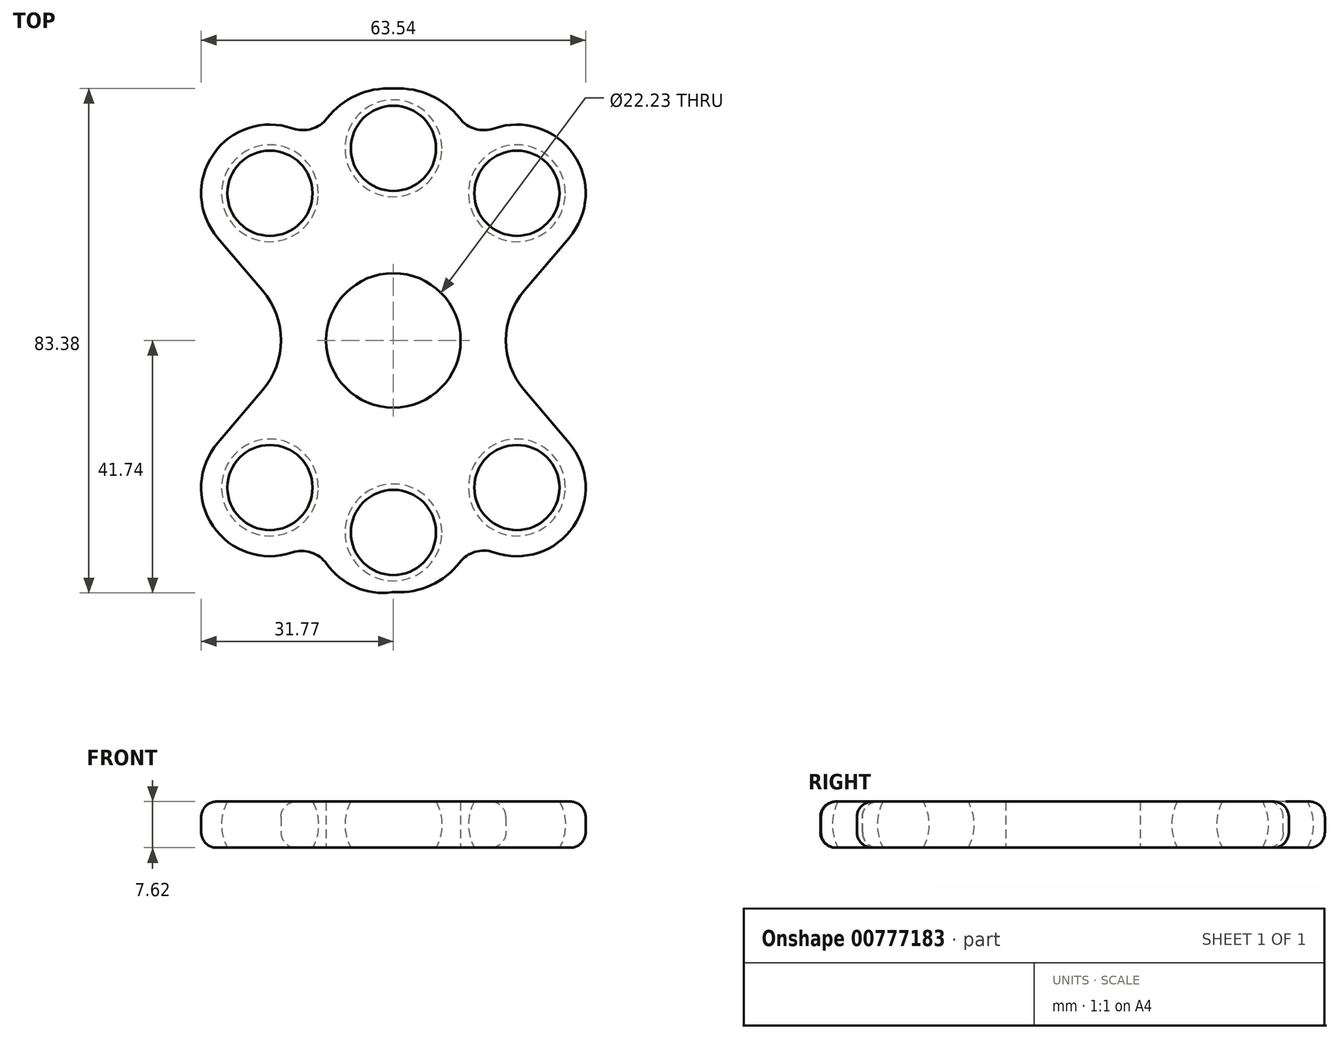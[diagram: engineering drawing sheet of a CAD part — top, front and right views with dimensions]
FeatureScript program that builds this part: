
annotation { "Feature Type Name" : "Feature", "Feature Type Description" : "" }
export const myFeature = defineFeature(function(context is Context, id is Id, definition is map)
    precondition{}
    {
        {
            var Q0;
            Q0=qCreatedBy(makeId("Top.planeOp"),FACE);
            var sketch = newSketch(context, id + "F0", { "sketchPlane" : qUnion([Q0])});
            skLineSegment(sketch, "E0", {"start": v(0, 31.75) * mm, "end": v(0, 0) * mm, "construction": true});
            skLineSegment(sketch, "E1", {"start": v(0, 0) * mm, "end": v(42.14, 0) * mm, "construction": true});
            skLineSegment(sketch, "E2", {"start": v(0, 31.75) * mm, "end": v(0, 57.84) * mm, "construction": true});
            skLineSegment(sketch, "E3", {"start": v(0, 0) * mm, "end": v(20.4, 24.32) * mm, "construction": true});
            skCircle(sketch, "E4", {"center": v(0, 0) * mm, "radius": 11.11 * mm});
            skArc(sketch, "E5", {"start": v(0, 23.75) * mm, "mid": v(8, 31.75) * mm, "end": v(0, 39.75) * mm, "construction": true});
            skCircle(sketch, "E6", {"center": v(20.4, 24.32) * mm, "radius": 8 * mm, "construction": true});
            skArc(sketch, "E7", {"start": v(29.05, 16.95) * mm, "mid": v(28.4, 32.38) * mm, "end": v(12.97, 32.9) * mm});
            skLineSegment(sketch, "E8", {"start": v(29.05, 16.95) * mm, "end": v(14.6, 0) * mm});
            skArc(sketch, "E9.MirrorCS", {"start": v(0, 23.75) * mm, "mid": v(-8, 31.75) * mm, "end": v(0, 39.75) * mm, "construction": true});
            skArc(sketch, "E10.MirrorC", {"start": v(-29.05, 16.95) * mm, "mid": v(-28.4, 32.38) * mm, "end": v(-12.97, 32.9) * mm});
            skCircle(sketch, "E11.MirrorC", {"center": v(-20.4, 24.32) * mm, "radius": 8 * mm, "construction": true});
            skLineSegment(sketch, "E12.MirrorCS", {"start": v(-29.05, 16.95) * mm, "end": v(-14.6, 0) * mm});
            skLineSegment(sketch, "E13.MirrorCS", {"start": v(29.05, -16.95) * mm, "end": v(14.6, 0) * mm});
            skLineSegment(sketch, "E14.MirrorCS", {"start": v(-29.05, -16.95) * mm, "end": v(-14.6, 0) * mm});
            skArc(sketch, "E15.MirrorC", {"start": v(-29.05, -16.95) * mm, "mid": v(-28.36, -32.43) * mm, "end": v(-12.87, -32.82) * mm});
            skArc(sketch, "E16.MirrorCS", {"start": v(-12.87, -32.82) * mm, "mid": v(-8.17, -39.75) * mm, "end": v(0, -41.6) * mm});
            skArc(sketch, "E17.MirrorC", {"start": v(29.05, -16.95) * mm, "mid": v(28.4, -32.38) * mm, "end": v(12.97, -32.9) * mm});
            skPoint(sketch, "E18.orphan", {"position": v(-8.46, 7.2) * mm});
            skPoint(sketch, "E19.orphan", {"position": v(-8.46, -7.2) * mm});
            skPoint(sketch, "E20.orphan", {"position": v(8.46, -7.2) * mm});
            skPoint(sketch, "E21.orphan", {"position": v(8.46, 7.2) * mm});
            skArc(sketch, "E22.trimOffspring", {"start": v(-12.97, 32.9) * mm, "mid": v(-7.98, 39.49) * mm, "end": v(0, 41.6) * mm});
            skArc(sketch, "E23.trimOffspring", {"start": v(12.97, 32.9) * mm, "mid": v(7.98, 39.49) * mm, "end": v(0, 41.6) * mm});
            skArc(sketch, "E24.trimOffspring", {"start": v(12.97, -32.9) * mm, "mid": v(7.98, -39.49) * mm, "end": v(0, -41.6) * mm});
            skPoint(sketch, "E25.MirrorCS.start.orphan", {"position": v(0, -19.05) * mm});
            skPoint(sketch, "E26.MirrorCS.start.orphan", {"position": v(0, 19.05) * mm});
            skSolve(sketch);
        }
        {
            var Q0;
            Q0=qSketchRegion(id+"F0",true);
            extrude(context, id + "F1", {"entities" : qUnion([Q0]), "endBound" : BoundingType.SYMMETRIC, "depth" : 7.62 * mm, "offsetDistance" : 25.4 * mm});
        }
        {
            var Q0;
            Q0=qCreatedBy(makeId("Front.planeOp"),FACE);
            var sketch = newSketch(context, id + "F2", { "sketchPlane" : qUnion([Q0])});
            skLineSegment(sketch, "E27", {"start": v(0, 0) * mm, "end": v(0, 93.09) * mm});
            skSolve(sketch);
        }
        {
            var Q0;
            Q0=sQuery(id+"F0.wireOp",VERTEX,"E3.end");
            var Q1;
            Q1=sQuery(id+"F2.wireOp",VERTEX,"E27.end");
            var Q2;
            Q2=sQuery(id+"F0.wireOp",VERTEX,"E0.end");
            cPlane(context, id + "F3", {"entities" : qUnion([Q0, Q1, Q2]), "cplaneType" : CPlaneType.THREE_POINT, "offset" : 25.4 * mm, "width" : 152.4 * mm, "height" : 152.4 * mm});
        }
        {
            var Q0;
            Q0=qCreatedBy(id+"F3.planeOp",FACE);
            var sketch = newSketch(context, id + "F4", { "sketchPlane" : qUnion([Q0])});
            skLineSegment(sketch, "E28", {"start": v(-31.75, 0) * mm, "end": v(-31.75, 45.58) * mm, "construction": true});
            skLineSegment(sketch, "E29", {"start": v(-31.75, 8) * mm, "end": v(-31.75, -8) * mm});
            skArc(sketch, "E30", {"start": v(-31.75, 8) * mm, "mid": v(-39.75, 0) * mm, "end": v(-31.75, -8) * mm});
            skSolve(sketch);
        }
        {
            var Q0;
            Q0=qSketchRegion(id+"F4",true);
            var Q1;
            Q1=sQuery(id+"F4.wireOp",EDGE,"E28");
            revolve(context, id + "F5", {"surfaceOperationType" : NewSurfaceOperationType.NEW, "entities" : qUnion([Q0]), "axis" : qUnion([Q1]), "revolveType" : RevolveType.FULL});
        }
        {
            var Q0;
            Q0=qCreatedBy(makeId("Right.planeOp"),FACE);
            var sketch = newSketch(context, id + "F6", { "sketchPlane" : qUnion([Q0])});
            skLineSegment(sketch, "E31", {"start": v(31.75, 0) * mm, "end": v(31.75, 41) * mm, "construction": true});
            skLineSegment(sketch, "E32", {"start": v(31.75, 8) * mm, "end": v(31.75, -8) * mm});
            skArc(sketch, "E33", {"start": v(31.75, -8) * mm, "mid": v(39.75, 0) * mm, "end": v(31.75, 8) * mm});
            skSolve(sketch);
        }
        {
            var Q0;
            Q0=makeQuery(id+"F6.imprint","IMPRINT",FACE,{"disambiguationData":[TD([[makeQuery(id+"F6.imprint","IMPRINT",EDGE,{"derivedFrom":sQuery(id+"F6.wireOp",EDGE,"E32")}),1.0]])]});
            var Q1;
            Q1=sQuery(id+"F6.wireOp",EDGE,"E31");
            revolve(context, id + "F7", {"surfaceOperationType" : NewSurfaceOperationType.NEW, "entities" : qUnion([Q0]), "axis" : qUnion([Q1]), "revolveType" : RevolveType.FULL});
        }
        {
            var Q0;
            Q0=makeQuery(id+"F5.opRevolve","SWEPT_BODY",BODY,{"disambiguationData":[OSD([sQuery(id+"F4.wireOp",EDGE,"E29"),sQuery(id+"F4.wireOp",EDGE,"E30")])]});
            var Q1;
            Q1=qCreatedBy(makeId("Right.planeOp"),FACE);
            mirror(context, id + "F8", {"entities" : qUnion([Q0]), "mirrorPlane" : qUnion([Q1])});
        }
        {
            var Q0;
            Q0=makeQuery(id+"F8.opPattern","COPY",BODY,{"derivedFrom":makeQuery(id+"F5.opRevolve","SWEPT_BODY",BODY,{"disambiguationData":[OSD([sQuery(id+"F4.wireOp",EDGE,"E29"),sQuery(id+"F4.wireOp",EDGE,"E30")])]}),"instanceName":"1"});
            var Q1;
            Q1=makeQuery(id+"F7.opRevolve","SWEPT_BODY",BODY,{"disambiguationData":[OSD([sQuery(id+"F6.wireOp",EDGE,"E32"),sQuery(id+"F6.wireOp",EDGE,"E33")])]});
            var Q2;
            Q2=makeQuery(id+"F5.opRevolve","SWEPT_BODY",BODY,{"disambiguationData":[OSD([sQuery(id+"F4.wireOp",EDGE,"E29"),sQuery(id+"F4.wireOp",EDGE,"E30")])]});
            var Q3;
            Q3=qCreatedBy(makeId("Front.planeOp"),FACE);
            mirror(context, id + "F9", {"entities" : qUnion([Q0, Q1, Q2]), "mirrorPlane" : qUnion([Q3])});
        }
        {
            var Q0;
            Q0=makeQuery(id+"F9.opPattern","COPY",BODY,{"derivedFrom":makeQuery(id+"F8.opPattern","COPY",BODY,{"derivedFrom":makeQuery(id+"F5.opRevolve","SWEPT_BODY",BODY,{"disambiguationData":[OSD([sQuery(id+"F4.wireOp",EDGE,"E29"),sQuery(id+"F4.wireOp",EDGE,"E30")])]}),"instanceName":"1"}),"instanceName":"1"});
            var Q1;
            Q1=makeQuery(id+"F9.opPattern","COPY",BODY,{"derivedFrom":makeQuery(id+"F7.opRevolve","SWEPT_BODY",BODY,{"disambiguationData":[OSD([sQuery(id+"F6.wireOp",EDGE,"E32"),sQuery(id+"F6.wireOp",EDGE,"E33")])]}),"instanceName":"1"});
            var Q2;
            Q2=makeQuery(id+"F9.opPattern","COPY",BODY,{"derivedFrom":makeQuery(id+"F5.opRevolve","SWEPT_BODY",BODY,{"disambiguationData":[OSD([sQuery(id+"F4.wireOp",EDGE,"E29"),sQuery(id+"F4.wireOp",EDGE,"E30")])]}),"instanceName":"1"});
            var Q3;
            Q3=makeQuery(id+"F8.opPattern","COPY",BODY,{"derivedFrom":makeQuery(id+"F5.opRevolve","SWEPT_BODY",BODY,{"disambiguationData":[OSD([sQuery(id+"F4.wireOp",EDGE,"E29"),sQuery(id+"F4.wireOp",EDGE,"E30")])]}),"instanceName":"1"});
            var Q4;
            Q4=makeQuery(id+"F5.opRevolve","SWEPT_BODY",BODY,{"disambiguationData":[OSD([sQuery(id+"F4.wireOp",EDGE,"E29"),sQuery(id+"F4.wireOp",EDGE,"E30")])]});
            var Q5;
            Q5=makeQuery(id+"F7.opRevolve","SWEPT_BODY",BODY,{"disambiguationData":[OSD([sQuery(id+"F6.wireOp",EDGE,"E32"),sQuery(id+"F6.wireOp",EDGE,"E33")])]});
            var Q6;
            Q6=makeQuery(id+"F1.opExtrude","SWEPT_BODY",BODY,{"disambiguationData":[OSD([sQuery(id+"F0.wireOp",EDGE,"E4"),sQuery(id+"F0.wireOp",EDGE,"E7"),sQuery(id+"F0.wireOp",EDGE,"E8"),sQuery(id+"F0.wireOp",EDGE,"E10.MirrorC"),sQuery(id+"F0.wireOp",EDGE,"E12.MirrorCS"),sQuery(id+"F0.wireOp",EDGE,"E13.MirrorCS"),sQuery(id+"F0.wireOp",EDGE,"E14.MirrorCS"),sQuery(id+"F0.wireOp",EDGE,"E15.MirrorC"),sQuery(id+"F0.wireOp",EDGE,"E16.MirrorCS"),sQuery(id+"F0.wireOp",EDGE,"E17.MirrorC"),sQuery(id+"F0.wireOp",EDGE,"E22.trimOffspring"),sQuery(id+"F0.wireOp",EDGE,"E23.trimOffspring"),sQuery(id+"F0.wireOp",EDGE,"E24.trimOffspring")])]});
            booleanBodies(context, id + "F10", {"operationType" : BooleanOperationType.SUBTRACTION, "tools" : qUnion([Q0, Q1, Q2, Q3, Q4, Q5]), "targets" : qUnion([Q6])});
        }
        {
            var Q0;
            Q0=makeQuery(id+"F1.opExtrude","SWEPT_EDGE",EDGE,{"disambiguationData":[OSD([sQuery(id+"F0.wireOp",EDGE,"E8"),sQuery(id+"F0.wireOp",EDGE,"E13.MirrorCS")])]});
            var Q1;
            Q1=makeQuery(id+"F1.opExtrude","SWEPT_EDGE",EDGE,{"disambiguationData":[OSD([sQuery(id+"F0.wireOp",EDGE,"E12.MirrorCS"),sQuery(id+"F0.wireOp",EDGE,"E14.MirrorCS")])]});
            fillet(context, id + "F11", {"entities" : qUnion([Q0, Q1]), "radius" : 12.7 * mm, "tangentPropagation" : true, "allowEdgeOverflow" : false});
        }
        {
            var Q0;
            Q0=makeQuery(id+"F1.opExtrude","SWEPT_EDGE",EDGE,{"disambiguationData":[OSD([sQuery(id+"F0.wireOp",EDGE,"E15.MirrorC"),sQuery(id+"F0.wireOp",EDGE,"E16.MirrorCS")])]});
            var Q1;
            Q1=makeQuery(id+"F1.opExtrude","SWEPT_EDGE",EDGE,{"disambiguationData":[OSD([sQuery(id+"F0.wireOp",EDGE,"E17.MirrorC"),sQuery(id+"F0.wireOp",EDGE,"E24.trimOffspring")])]});
            var Q2;
            Q2=makeQuery(id+"F1.opExtrude","SWEPT_EDGE",EDGE,{"disambiguationData":[OSD([sQuery(id+"F0.wireOp",EDGE,"E7"),sQuery(id+"F0.wireOp",EDGE,"E23.trimOffspring")])]});
            var Q3;
            Q3=makeQuery(id+"F1.opExtrude","SWEPT_EDGE",EDGE,{"disambiguationData":[OSD([sQuery(id+"F0.wireOp",EDGE,"E10.MirrorC"),sQuery(id+"F0.wireOp",EDGE,"E22.trimOffspring")])]});
            fillet(context, id + "F12", {"entities" : qUnion([Q0, Q1, Q2, Q3]), "radius" : 5.08 * mm, "tangentPropagation" : true, "allowEdgeOverflow" : false});
        }
        {
            var Q0;
            Q0=makeQuery(id+"F1.opExtrude","SWEPT_FACE",FACE,{"disambiguationData":[OSD([sQuery(id+"F0.wireOp",EDGE,"E10.MirrorC")])]});
            var Q1;
            Q1=makeQuery(id+"F1.opExtrude","SWEPT_FACE",FACE,{"disambiguationData":[OSD([sQuery(id+"F0.wireOp",EDGE,"E12.MirrorCS")])]});
            var Q2;
            Q2=makeQuery(id+"F11.opFillet","BLEND_FACE",FACE,{"disambiguationData":[OSD([sQuery(id+"F0.wireOp",EDGE,"E12.MirrorCS"),sQuery(id+"F0.wireOp",EDGE,"E14.MirrorCS")])]});
            var Q3;
            Q3=makeQuery(id+"F1.opExtrude","SWEPT_FACE",FACE,{"disambiguationData":[OSD([sQuery(id+"F0.wireOp",EDGE,"E14.MirrorCS")])]});
            var Q4;
            Q4=makeQuery(id+"F1.opExtrude","SWEPT_FACE",FACE,{"disambiguationData":[OSD([sQuery(id+"F0.wireOp",EDGE,"E15.MirrorC")])]});
            var Q5;
            Q5=makeQuery(id+"F12.opFillet","BLEND_FACE",FACE,{"disambiguationData":[OSD([sQuery(id+"F0.wireOp",EDGE,"E15.MirrorC"),sQuery(id+"F0.wireOp",EDGE,"E16.MirrorCS")])]});
            var Q6;
            Q6=makeQuery(id+"F1.opExtrude","SWEPT_FACE",FACE,{"disambiguationData":[OSD([sQuery(id+"F0.wireOp",EDGE,"E16.MirrorCS")])]});
            var Q7;
            Q7=makeQuery(id+"F1.opExtrude","SWEPT_FACE",FACE,{"disambiguationData":[OSD([sQuery(id+"F0.wireOp",EDGE,"E24.trimOffspring")])]});
            var Q8;
            Q8=makeQuery(id+"F12.opFillet","BLEND_FACE",FACE,{"disambiguationData":[OSD([sQuery(id+"F0.wireOp",EDGE,"E17.MirrorC"),sQuery(id+"F0.wireOp",EDGE,"E24.trimOffspring")])]});
            var Q9;
            Q9=makeQuery(id+"F1.opExtrude","SWEPT_FACE",FACE,{"disambiguationData":[OSD([sQuery(id+"F0.wireOp",EDGE,"E17.MirrorC")])]});
            var Q10;
            Q10=makeQuery(id+"F1.opExtrude","SWEPT_FACE",FACE,{"disambiguationData":[OSD([sQuery(id+"F0.wireOp",EDGE,"E13.MirrorCS")])]});
            var Q11;
            Q11=makeQuery(id+"F11.opFillet","BLEND_FACE",FACE,{"disambiguationData":[OSD([sQuery(id+"F0.wireOp",EDGE,"E8"),sQuery(id+"F0.wireOp",EDGE,"E13.MirrorCS")])]});
            var Q12;
            Q12=makeQuery(id+"F1.opExtrude","SWEPT_FACE",FACE,{"disambiguationData":[OSD([sQuery(id+"F0.wireOp",EDGE,"E8")])]});
            var Q13;
            Q13=makeQuery(id+"F1.opExtrude","SWEPT_FACE",FACE,{"disambiguationData":[OSD([sQuery(id+"F0.wireOp",EDGE,"E7")])]});
            var Q14;
            Q14=makeQuery(id+"F1.opExtrude","SWEPT_FACE",FACE,{"disambiguationData":[OSD([sQuery(id+"F0.wireOp",EDGE,"E22.trimOffspring")])]});
            var Q15;
            Q15=makeQuery(id+"F12.opFillet","BLEND_FACE",FACE,{"disambiguationData":[OSD([sQuery(id+"F0.wireOp",EDGE,"E10.MirrorC"),sQuery(id+"F0.wireOp",EDGE,"E22.trimOffspring")])]});
            var Q16;
            Q16=makeQuery(id+"F1.opExtrude","SWEPT_FACE",FACE,{"disambiguationData":[OSD([sQuery(id+"F0.wireOp",EDGE,"E23.trimOffspring")])]});
            var Q17;
            Q17=makeQuery(id+"F12.opFillet","BLEND_FACE",FACE,{"disambiguationData":[OSD([sQuery(id+"F0.wireOp",EDGE,"E7"),sQuery(id+"F0.wireOp",EDGE,"E23.trimOffspring")])]});
            fillet(context, id + "F13", {"entities" : qUnion([Q0, Q1, Q2, Q3, Q4, Q5, Q6, Q7, Q8, Q9, Q10, Q11, Q12, Q13, Q14, Q15, Q16, Q17]), "radius" : 2.54 * mm, "tangentPropagation" : true, "allowEdgeOverflow" : false});
        }
    });
